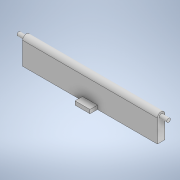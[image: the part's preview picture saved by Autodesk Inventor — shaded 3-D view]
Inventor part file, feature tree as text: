
AUTODESK INVENTOR PART (.ipt)
format: ipt  version: 2022 (Build 260153000, 153)  size: 123,904 bytes
history: native  units: in
note: dims shown in document units (in); Inventor stores cm internally (conversion verified against a paired STEP export)
features: extrude x4, sketch x4, fillet x1
ambient origin geometry x8: Origin, YZ Plane, XZ Plane, XY Plane, X Axis, Y Axis, Z Axis, Center Point
bodies: Solid1 (feature_tree)
feature tree (9):
  extrude  "Extrusion1"  Depth=0.25in TaperAngle=0.0deg
  extrude  "Extrusion2"  Depth=0.125in
  extrude  "Extrusion3"  Depth=0.25in TaperAngle=0.0deg
  extrude  "Extrusion4"  Depth=0.125in
  fillet  "Fillet1"  Radius=2.0in
  sketch  "Sketch1"  dims[d0=4.5in d1=0.25in d2=0.0in]
  sketch  "Sketch2"  dims[d3=0.125in d4=0.125in]
  sketch  "Sketch3"  dims[d5=0.25in d6=0.0in d7=0.25in d8=0.0in]
  sketch  "Sketch4"  dims[d9=0.5in d10=0.125in d11=2.0in d12=0.25in d13=0.0in d14=0.875in d15=0.125in]
